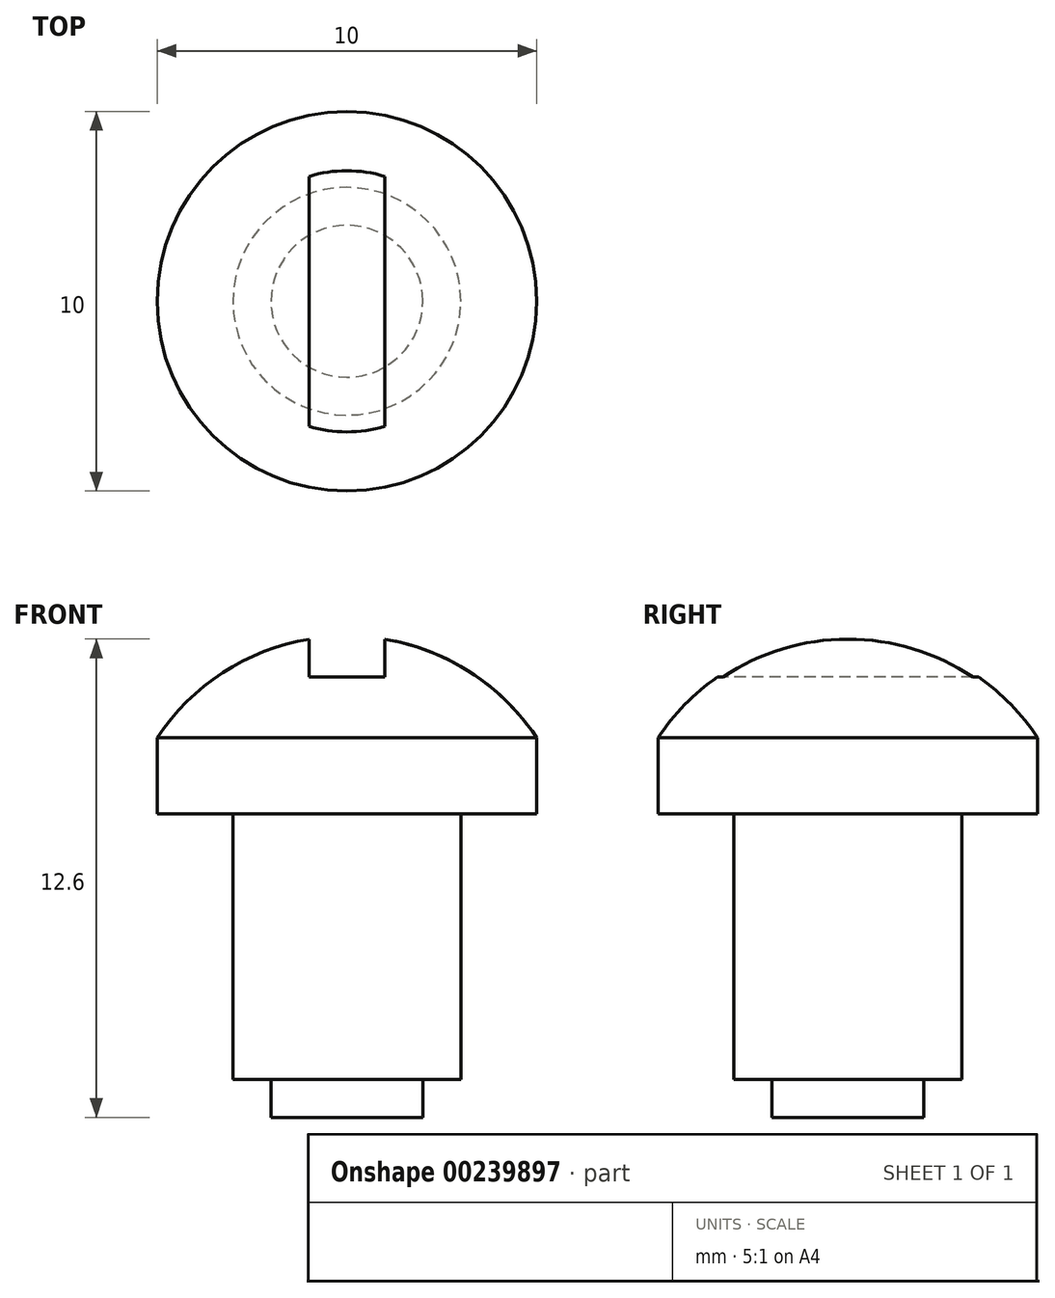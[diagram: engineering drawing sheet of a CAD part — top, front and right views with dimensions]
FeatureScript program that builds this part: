
annotation { "Feature Type Name" : "Feature", "Feature Type Description" : "" }
export const myFeature = defineFeature(function(context is Context, id is Id, definition is map)
    precondition{}
    {
        {
            var Q0;
            Q0=qCreatedBy(makeId("Front.planeOp"),FACE);
            var sketch = newSketch(context, id + "F0", { "sketchPlane" : qUnion([Q0])});
            skLineSegment(sketch, "E0.top", {"start": v(0, 0) * mm, "end": v(-2, 0) * mm});
            skLineSegment(sketch, "E0.right", {"start": v(-2, 1) * mm, "end": v(-2, 0) * mm});
            skPoint(sketch, "E0.middle", {"position": v(0, 0) * mm});
            skLineSegment(sketch, "E1", {"start": v(-2, 1) * mm, "end": v(-3, 1) * mm});
            skLineSegment(sketch, "E2", {"start": v(-3, 1) * mm, "end": v(-3, 8) * mm});
            skLineSegment(sketch, "E3", {"start": v(-3, 8) * mm, "end": v(-5, 8) * mm});
            skLineSegment(sketch, "E4", {"start": v(-5, 8) * mm, "end": v(-5, 10) * mm});
            skArc(sketch, "E5", {"start": v(0, 12.68) * mm, "mid": v(-2.84, 11.97) * mm, "end": v(-5, 10) * mm});
            skLineSegment(sketch, "E6", {"start": v(0, 12.68) * mm, "end": v(0, 0) * mm});
            skSolve(sketch);
        }
        {
            var Q0;
            Q0=makeQuery(id+"F0.imprint","IMPRINT",FACE,{"disambiguationData":[TD([[makeQuery(id+"F0.imprint","IMPRINT",EDGE,{"derivedFrom":sQuery(id+"F0.wireOp",EDGE,"E0.top")}),-1.0]])]});
            var Q1;
            {var subQ0=sQuery(id+"F0.wireOp",EDGE,"QI7UCKIY-cN2F-H26A-T2d8-03zfSCD3YwDe");Q1=makeQuery(id+"F0.imprint","IMPRINT",FACE,{"disambiguationData":[TD([[makeQuery(id+"F0.imprint","IMPRINT",EDGE,{"derivedFrom":subQ0}),-1.0]])]});}
            var Q2;
            Q2=sQuery(id+"F0.wireOp",EDGE,"E6");
            revolve(context, id + "F1", {"entities" : qUnion([Q0, Q1]), "axis" : qUnion([Q2]), "revolveType" : RevolveType.FULL});
        }
        {
            var Q0;
            Q0=qCreatedBy(makeId("Front.planeOp"),FACE);
            var sketch = newSketch(context, id + "F2", { "sketchPlane" : qUnion([Q0])});
            skArc(sketch, "E7.0", {"start": v(0, 12.68) * mm, "mid": v(-0.5, 12.66) * mm, "end": v(-1, 12.6) * mm});
            skLineSegment(sketch, "E8", {"start": v(-1, 12.6) * mm, "end": v(-1, 11.6) * mm});
            skLineSegment(sketch, "E9", {"start": v(-1, 11.6) * mm, "end": v(0, 11.6) * mm});
            skLineSegment(sketch, "E10", {"start": v(0, 13.94) * mm, "end": v(0, 10.89) * mm, "construction": true});
            skPoint(sketch, "E11.orphan", {"position": v(-5, 10) * mm});
            skLineSegment(sketch, "E12.MirrorCS", {"start": v(1, 11.6) * mm, "end": v(0, 11.6) * mm});
            skArc(sketch, "E13.MirrorCS", {"start": v(0, 12.68) * mm, "mid": v(0.5, 12.66) * mm, "end": v(1, 12.6) * mm});
            skLineSegment(sketch, "E14.MirrorCS", {"start": v(1, 12.6) * mm, "end": v(1, 11.6) * mm});
            skSolve(sketch);
        }
        {
            var Q0;
            Q0 = qSketchRegion(id + "F2", true);
            extrude(context, id + "F3", {"entities" : qUnion([Q0]), "operationType" : NewBodyOperationType.REMOVE, "endBound" : BoundingType.SYMMETRIC, "oppositeDirection" : true, "depth" : 10 * mm});
        }
    });
